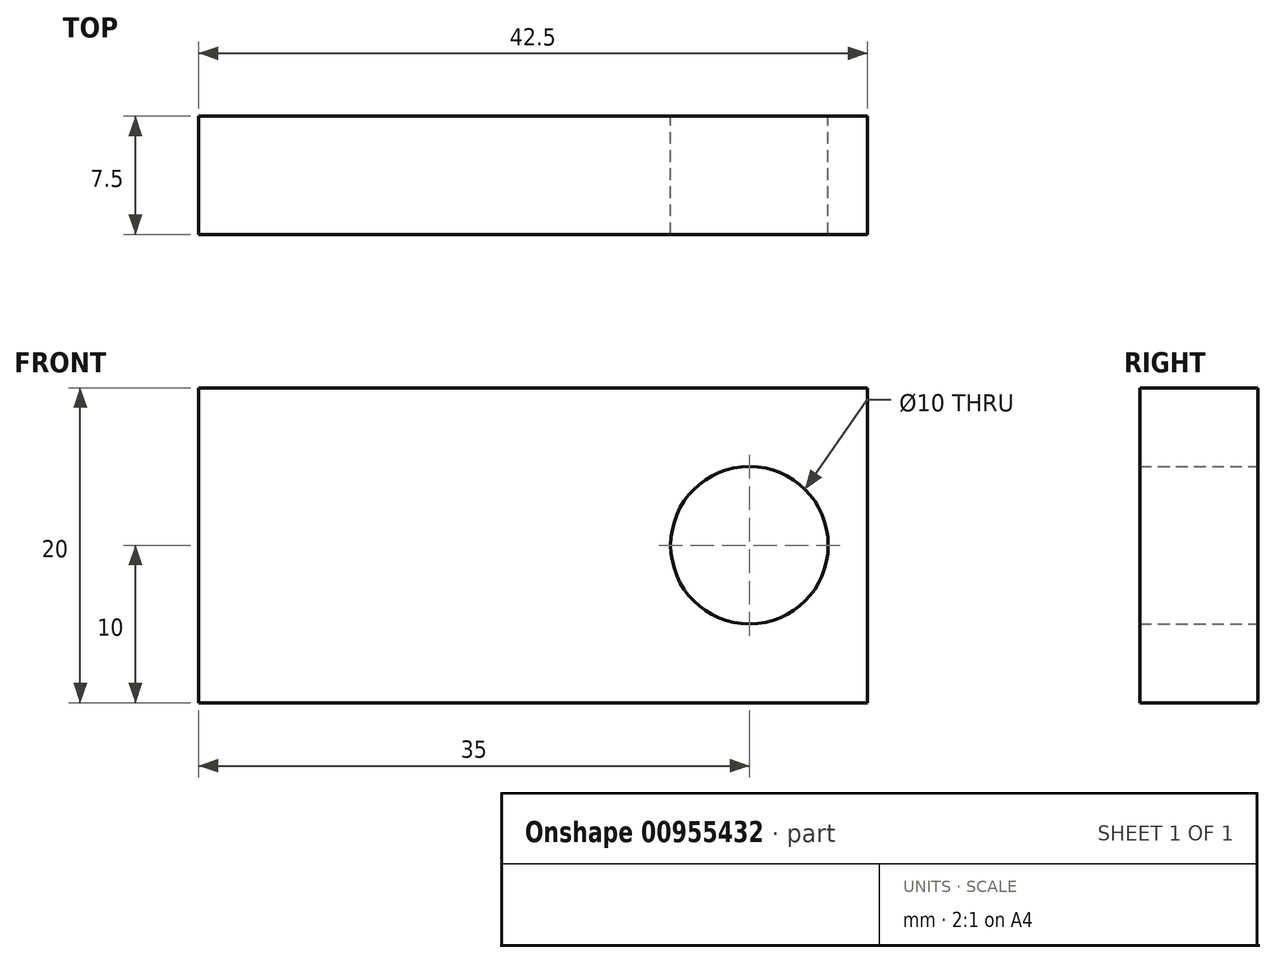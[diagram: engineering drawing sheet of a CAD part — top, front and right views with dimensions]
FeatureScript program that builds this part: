
annotation { "Feature Type Name" : "Feature", "Feature Type Description" : "" }
export const myFeature = defineFeature(function(context is Context, id is Id, definition is map)
    precondition{}
    {
        {
            var Q0;
            Q0=qCreatedBy(makeId("Front.planeOp"),FACE);
            var sketch = newSketch(context, id + "F0", { "sketchPlane" : qUnion([Q0])});
            skLineSegment(sketch, "E0.bottom", {"start": v(21.25, 10) * mm, "end": v(-21.25, 10) * mm});
            skLineSegment(sketch, "E0.top", {"start": v(21.25, -10) * mm, "end": v(-21.25, -10) * mm});
            skLineSegment(sketch, "E0.left", {"start": v(21.25, 10) * mm, "end": v(21.25, -10) * mm});
            skLineSegment(sketch, "E0.right", {"start": v(-21.25, 10) * mm, "end": v(-21.25, -10) * mm});
            skPoint(sketch, "E0.middle", {"position": v(0, 0) * mm});
            skCircle(sketch, "E1", {"center": v(13.75, 0) * mm, "radius": 5 * mm});
            skSolve(sketch);
        }
        {
            var Q0;
            Q0=makeQuery(id+"F0.imprint","IMPRINT",FACE,{"disambiguationData":[TD([[makeQuery(id+"F0.imprint","IMPRINT",EDGE,{"derivedFrom":sQuery(id+"F0.wireOp",EDGE,"E0.bottom")}),1.0]])]});
            extrude(context, id + "F1", {"entities" : qUnion([Q0]), "depth" : 7.5 * mm, "offsetDistance" : 25 * mm});
        }
    });
